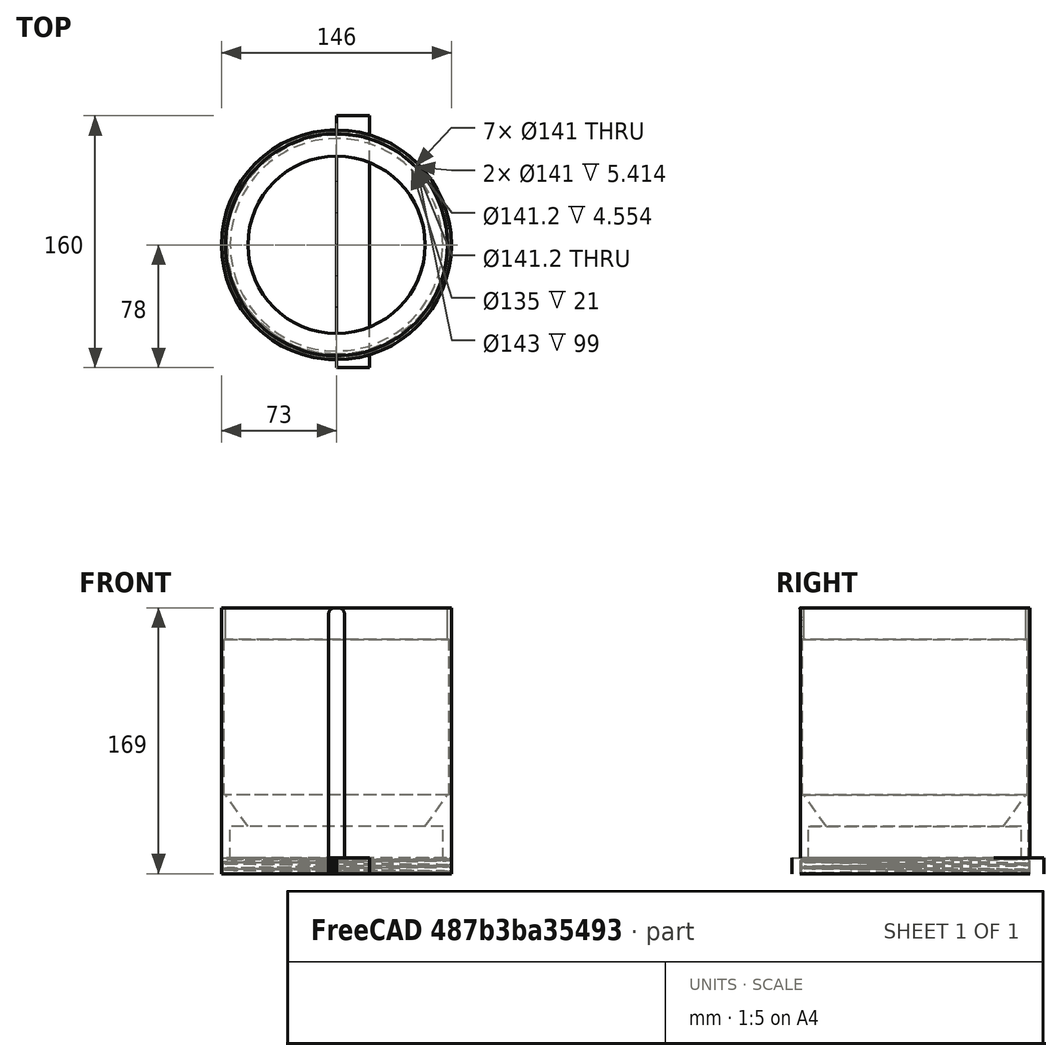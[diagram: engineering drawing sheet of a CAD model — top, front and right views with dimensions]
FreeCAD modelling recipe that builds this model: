
FCSTD DOCUMENT  (FreeCAD 0.19R24291 (Git))
Label: x_nadoba
License: All rights reserved
LicenseURL: http://en.wikipedia.org/wiki/All_rights_reserved
objects: Part::Cylinder×6, Part::MultiFuse×4, Part::Box×3, Part::Cut×3, Part::FeaturePython×2, Part::Feature×2, Part::Fillet×2, Part::Cone×1
note: 23 computed .brp shape members not serialized (recipe doc carries the construction recipe); baked Part::Feature solids carry a one-line shape summary decoded from their .brp

FEATURE [Part::FeaturePython] Tube  # WARN: FeaturePython — macro-defined, semantics opaque (R4)
  AttacherType = Attacher::AttachEngine3D
  Height = 50
  InnerRadius = 40
  OuterRadius = 73
FEATURE [Part::Cylinder] Cylinder
  Angle = 360
  AttacherType = Attacher::AttachEngine3D
  Height = 9
  Radius = 70.6
FEATURE [Part::Cone] Cone
  Angle = 360
  AttacherType = Attacher::AttachEngine3D
  Height = 50
  Radius1 = 35
  Radius2 = 70.5
FEATURE [Part::FeaturePython] Tube001  # WARN: FeaturePython — macro-defined, semantics opaque (R4)
  AttacherType = Attacher::AttachEngine3D
  Height = 120
  InnerRadius = 70.5
  OuterRadius = 73
  Placement = pos=(0,0,49) rot=(0,0,1;0rad)
FEATURE [Part::MultiFuse] Fusion001
  Shapes = -> [Tube001,Tube]
FEATURE [Part::Cylinder] Cylinder001
  Angle = 360
  AttacherType = Attacher::AttachEngine3D
  Height = 40
  Placement = pos=(0,0,10) rot=(0,0,1;0rad)
  Radius = 80
FEATURE [Part::Cylinder] Cylinder002
  Angle = 360
  AttacherType = Attacher::AttachEngine3D
  Height = 80
  Placement = pos=(0,0,169) rot=(0,0,1;0rad)
  Radius = 80
FEATURE [Part::Cylinder] Cylinder003
  Angle = 360
  AttacherType = Attacher::AttachEngine3D
  Height = 128
  Placement = pos=(0,0,-128) rot=(0,0,1;0rad)
  Radius = 80
FEATURE [Part::MultiFuse] Fusion003
  Shapes = -> [Cylinder003,Cylinder001]
FEATURE [Part::Box] Box  label="Cube"
  AttacherType = Attacher::AttachEngine3D
  Height = 10
  Length = 21
  Placement = pos=(0,-78,0) rot=(0,0,1;0rad)
  Width = 160
FEATURE [Part::Feature] Sweep003003  label="Sweep_out2 71a"
  Placement = pos=(0,0,-25) rot=(0,0,1;0rad)
  shape: bbox 166.1 x 177 x 68.7 mm, 18 faces (baked)
FEATURE [Part::Cut] Cut002
  Base = -> Sweep003003
  Tool = -> Fusion003
FEATURE [Part::Feature] Sweep003004  label="Sweep_out2 71a001"
  Placement = pos=(0,0,149) rot=(0,0,1;0rad)
  shape: bbox 166.1 x 177 x 68.7 mm, 18 faces (baked)
FEATURE [Part::Cut] Cut003
  Base = -> Sweep003004
  Tool = -> Cylinder002
FEATURE [Part::Cylinder] Cylinder004
  Angle = 360
  AttacherType = Attacher::AttachEngine3D
  Height = 21
  Placement = pos=(0,0,9) rot=(0,0,1;0rad)
  Radius = 67.5
FEATURE [Part::Box] Box001  label="Cube001"
  AttacherType = Attacher::AttachEngine3D
  Height = 169
  Length = 10
  Placement = pos=(-5,-82,0) rot=(0,0,1;0rad)
  Width = 10
FEATURE [Part::Box] Box002  label="Cube002"
  AttacherType = Attacher::AttachEngine3D
  Height = 169
  Length = 10
  Placement = pos=(-5,72,0) rot=(0,0,1;0rad)
  Width = 10
FEATURE [Part::Fillet] Fillet
  Base = -> Box001
  Edges = 7 edges: [Edge1 r=4,Edge2 r=4,Edge5 r=4,Edge6 r=4,Edge8 r=1,Edge9 r=9.5,Edge10 r=9.5]
FEATURE [Part::Fillet] Fillet001
  Base = -> Box002
  Edges = 8 edges: [Edge2 r=4,Edge3 r=4,Edge4 r=1,Edge6 r=4,Edge7 r=4,Edge8 r=1,Edge11 r=9.5,Edge12 r=9.5]
FEATURE [Part::Cylinder] Cylinder005  label="Cylinder005_tensia_stena"
  Angle = 360
  AttacherType = Attacher::AttachEngine3D
  Height = 99
  Placement = pos=(0,0,50) rot=(0,0,1;0rad)
  Radius = 71.5
FEATURE [Part::MultiFuse] Fusion
  Shapes = -> [Cylinder,Cone,Cylinder004,Cylinder005]
FEATURE [Part::Cut] Cut
  Base = -> Fusion001
  Tool = -> Fusion
FEATURE [Part::MultiFuse] Fusion002
  Shapes = -> [Cut,Cut002,Cut003,Fillet,Fillet001]
